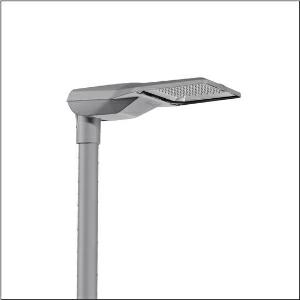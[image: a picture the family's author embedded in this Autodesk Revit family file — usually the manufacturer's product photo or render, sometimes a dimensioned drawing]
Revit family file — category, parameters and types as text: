
# Revit family: streetlight_sl_21_iq_midi___st0_5a_5xe3b31g08mb_2812
name_source: partatom
category: Lighting Fixtures
units: mm (PartAtom-declared; Revit-internal decimal feet)

## family parameters
Cut with Voids When Loaded = No
Host = Face
Light Source = No
Part Type = Normal
Room Calculation Point = No
Round Connector Dimension = Use Diameter
Shared = No

## types (1)
- --- (1 x LED, 19500 lm, 146.7 W, 3000K)
    Apparent Load = 147 VA
    CIE Flux Codes = 41 75 97 100 100
    Color Rendering = 70
    Color Temperature = 3000K
    Default Elevation = 1800 mm
    Description = Streetlight SL 21 iQ midi, mast luminaire, primary light control with lens, of PMMA, primary optical cover: cover, of toughened safety glass, transparent, light distribution: ST0.5a, light emission: direct distribution, primary light characteristic: asymmetric, installation type: post-top, side-entry, LED, High Power LED, rated luminous flux: 19.500lm, luminous efficacy: 133lm/W, light colour: 730, colour temperature: 3000K, control: Street-Remote, Auto-Match, Temp-Guard, Lumen-Switch, Night-Set, Smart-Wire, Light-Fading, Desk-Remote (wireless, voltage-free reading and setting of iQ features in the workshop via application-optimized NFC function/RFID function), optimised constant luminous flux control (CLO 2.0), presetting dimming linear, mains connection: 230..240V, AC, 50/60Hz, start of lifetime: 147W, end of service life: 161W, reduction: 62W, luminaire housing, of diecast aluminium, powder-coated, Siteco® metallic grey (DB 702S), corrosivity category C5 mid according to DIN EN ISO 12944, please order mast flange separately, inclination adjustable: 0°, 5°, 10°, 15°, sealing non-destructively replaceable, multi-level sealing system, length: 644mm, width: 335mm, height: 110mm, mast flange for spigot size: 42mm (side-entry): 5XC10008XM4, 60/48mm (side-entry/post-top): 5XC10108XM2, 76/60mm (side-entry/post-top): 5XC10108XM1, protection rating (complete): IP66, insulation class (complete): insulation class II (safety insulation), certification: CE, ENEC, ENEC+, VDE, impact resistance: IK09, permissible operating ambient temperature for outdoor applications: -40..+50°C, standard-compliant lighting for roads and squares, packaging unit: 1 piece

Light Distribution: ST0.5a
    Height = 111 mm
    Lamp = 1 x LED
    Lamp Light Flux = 19500 lm
    Lamp Power = 146.7 W
    Lamp count = 1
    Length = 644 mm
    Luminous efficacy = 133 lm/W
    Manufacturer = Siteco
    ModVariant = No
    Model = 5XE3B31G08MB
    Number of Poles = 1
    OnlyDefault = Yes
    Power Factor = 1
    Product Name = Streetlight SL 21 iQ midi | ST0.5a
    Product group = mast luminaire | pylon top
    ProductGroupID = 6100
    Protection Class = Protection class II
    Protection Degree = IP 66
    RLX_Detail_Level = 1
    RLX_Emergency_Light_Flux = 0 lm
    RLX_Emergency_Type = 0
    RLX_Emergency_Type_DB = No
    RlxData = <blob elided: 101801 chars, md5=3889d846>
    Socket = socket
    Standby Power = 0 W
    System Light Flux = 19499 lm
    System Power = 147 W
    Type Comments = factory setting: luminous flux: 100 % | dim-lin: 254 | 753 mA
    Type Image = l_1004298.jpg
    URL = http://relux.com
    VarID = @adj_126131
    Voltage = 0 V
    Weight = 0.00 kg
    Width = 336 mm

## geometry (parser evidence)
native form markers: Blend x4, Sweep x10
no freeform markers — native parametric forms only
